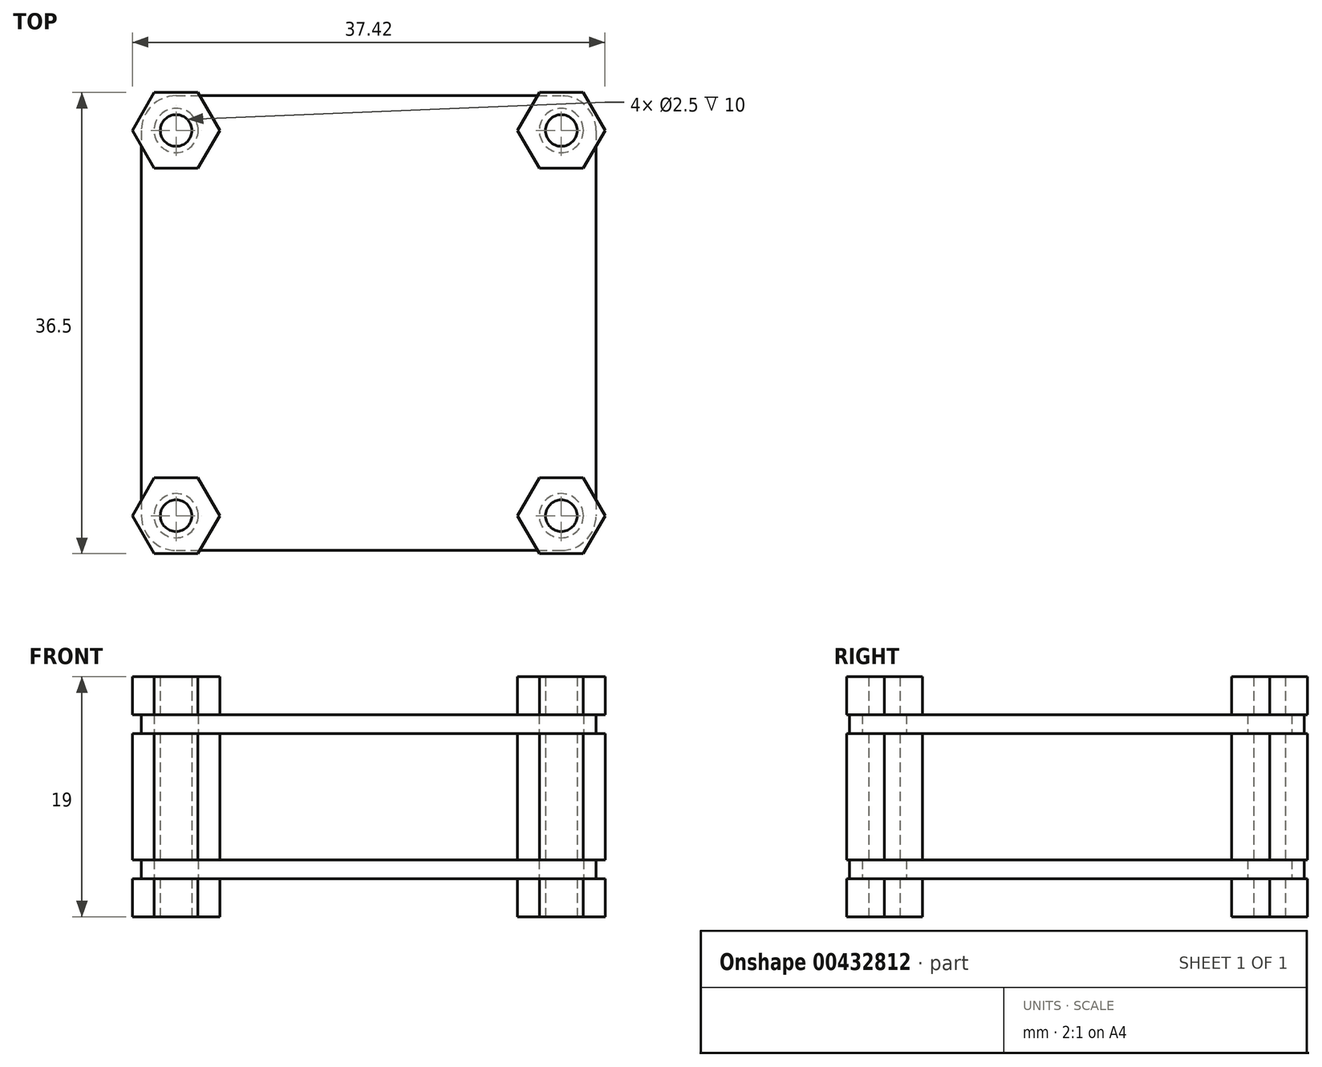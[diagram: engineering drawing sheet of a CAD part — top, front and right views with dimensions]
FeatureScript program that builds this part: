
annotation { "Feature Type Name" : "Feature", "Feature Type Description" : "" }
export const myFeature = defineFeature(function(context is Context, id is Id, definition is map)
    precondition{}
    {
        {
            var Q0;
            Q0=qCreatedBy(makeId("Top.planeOp"),FACE);
            var sketch = newSketch(context, id + "F0", { "sketchPlane" : qUnion([Q0])});
            skLineSegment(sketch, "E0.bottom", {"start": v(-15.25, 18) * mm, "end": v(15.25, 18) * mm});
            skLineSegment(sketch, "E0.top", {"start": v(-15.25, -18) * mm, "end": v(15.25, -18) * mm});
            skLineSegment(sketch, "E0.left", {"start": v(-18, 15.25) * mm, "end": v(-18, -15.25) * mm});
            skLineSegment(sketch, "E0.right", {"start": v(18, 15.25) * mm, "end": v(18, -15.25) * mm});
            skPoint(sketch, "E0.middle", {"position": v(0, 0) * mm});
            skPoint(sketch, "E1.visualSharp", {"position": v(-18, 18) * mm});
            skArc(sketch, "E1.filletArc", {"start": v(-15.25, 18) * mm, "mid": v(-17.2, 17.2) * mm, "end": v(-18, 15.25) * mm});
            skPoint(sketch, "E2.visualSharp", {"position": v(18, 18) * mm});
            skArc(sketch, "E2.filletArc", {"start": v(18, 15.25) * mm, "mid": v(17.2, 17.2) * mm, "end": v(15.25, 18) * mm});
            skPoint(sketch, "E3.visualSharp", {"position": v(18, -18) * mm});
            skArc(sketch, "E3.filletArc", {"start": v(15.25, -18) * mm, "mid": v(17.2, -17.2) * mm, "end": v(18, -15.25) * mm});
            skPoint(sketch, "E4.visualSharp", {"position": v(-18, -18) * mm});
            skArc(sketch, "E4.filletArc", {"start": v(-18, -15.25) * mm, "mid": v(-17.2, -17.2) * mm, "end": v(-15.25, -18) * mm});
            skCircle(sketch, "E5", {"center": v(-15.25, 15.25) * mm, "radius": 1.75 * mm});
            skCircle(sketch, "E6", {"center": v(15.25, 15.25) * mm, "radius": 1.75 * mm});
            skCircle(sketch, "E7", {"center": v(15.25, -15.25) * mm, "radius": 1.75 * mm});
            skCircle(sketch, "E8", {"center": v(-15.25, -15.25) * mm, "radius": 1.75 * mm});
            skSolve(sketch);
        }
        {
            var Q0;
            Q0=makeQuery(id+"F0.imprint","IMPRINT",FACE,{"disambiguationData":[TD([[makeQuery(id+"F0.imprint","IMPRINT",EDGE,{"derivedFrom":sQuery(id+"F0.wireOp",EDGE,"E0.bottom")}),-1.0]])]});
            extrude(context, id + "F1", {"entities" : qUnion([Q0]), "depth" : 4.5 * mm, "hasSecondDirection" : true, "secondDirectionOppositeDirection" : false, "secondDirectionDepth" : 3 * mm});
        }
        {
            var Q0;
            Q0=makeQuery(id+"F0.imprint","IMPRINT",FACE,{"disambiguationData":[TD([[makeQuery(id+"F0.imprint","IMPRINT",EDGE,{"derivedFrom":sQuery(id+"F0.wireOp",EDGE,"E0.bottom")}),-1.0]])]});
            extrude(context, id + "F2", {"entities" : qUnion([Q0]), "depth" : 16 * mm, "hasSecondDirection" : true, "secondDirectionOppositeDirection" : false, "secondDirectionDepth" : 14.5 * mm});
        }
        {
            var Q0;
            Q0=qCreatedBy(makeId("Top.planeOp"),FACE);
            var sketch = newSketch(context, id + "F3", { "sketchPlane" : qUnion([Q0])});
            skCircle(sketch, "E9.cCircle", {"center": v(-15.25, -15.25) * mm, "radius": 3 * mm, "construction": true});
            skLineSegment(sketch, "E9.0", {"start": v(-11.79, -15.25) * mm, "end": v(-13.52, -18.25) * mm});
            skLineSegment(sketch, "E9.1", {"start": v(-13.52, -18.25) * mm, "end": v(-16.98, -18.25) * mm});
            skLineSegment(sketch, "E9.2", {"start": v(-16.98, -18.25) * mm, "end": v(-18.71, -15.25) * mm});
            skLineSegment(sketch, "E9.3", {"start": v(-18.71, -15.25) * mm, "end": v(-16.98, -12.25) * mm});
            skLineSegment(sketch, "E9.4", {"start": v(-16.98, -12.25) * mm, "end": v(-13.52, -12.25) * mm});
            skLineSegment(sketch, "E9.5", {"start": v(-13.52, -12.25) * mm, "end": v(-11.79, -15.25) * mm});
            skPoint(sketch, "E9.0.midPoint", {"position": v(-12.65, -16.75) * mm});
            skLineSegment(sketch, "E10.MirrorCS", {"start": v(16.98, -12.25) * mm, "end": v(13.52, -12.25) * mm});
            skLineSegment(sketch, "E11.MirrorCS", {"start": v(18.71, -15.25) * mm, "end": v(16.98, -12.25) * mm});
            skLineSegment(sketch, "E12.MirrorCS", {"start": v(16.98, -18.25) * mm, "end": v(18.71, -15.25) * mm});
            skLineSegment(sketch, "E13.MirrorCS", {"start": v(13.52, -18.25) * mm, "end": v(16.98, -18.25) * mm});
            skLineSegment(sketch, "E14.MirrorCS", {"start": v(11.79, -15.25) * mm, "end": v(13.52, -18.25) * mm});
            skPoint(sketch, "E15.MirrorP", {"position": v(12.65, -16.75) * mm});
            skLineSegment(sketch, "E16.MirrorCS", {"start": v(13.52, -12.25) * mm, "end": v(11.79, -15.25) * mm});
            skCircle(sketch, "E17.MirrorC", {"center": v(15.25, -15.25) * mm, "radius": 3 * mm, "construction": true});
            skLineSegment(sketch, "E18.MirrorCS", {"start": v(11.79, 15.25) * mm, "end": v(13.52, 18.25) * mm});
            skLineSegment(sketch, "E19.MirrorCS", {"start": v(13.52, 18.25) * mm, "end": v(16.98, 18.25) * mm});
            skLineSegment(sketch, "E20.MirrorCS", {"start": v(16.98, 18.25) * mm, "end": v(18.71, 15.25) * mm});
            skLineSegment(sketch, "E21.MirrorCS", {"start": v(16.98, 12.25) * mm, "end": v(13.52, 12.25) * mm});
            skLineSegment(sketch, "E22.MirrorCS", {"start": v(-11.79, 15.25) * mm, "end": v(-13.52, 18.25) * mm});
            skLineSegment(sketch, "E23.MirrorCS", {"start": v(-13.52, 18.25) * mm, "end": v(-16.98, 18.25) * mm});
            skLineSegment(sketch, "E24.MirrorCS", {"start": v(-16.98, 18.25) * mm, "end": v(-18.71, 15.25) * mm});
            skLineSegment(sketch, "E25.MirrorCS", {"start": v(-16.98, 12.25) * mm, "end": v(-13.52, 12.25) * mm});
            skLineSegment(sketch, "E26.MirrorCS", {"start": v(-13.52, 12.25) * mm, "end": v(-11.79, 15.25) * mm});
            skPoint(sketch, "E27.MirrorP", {"position": v(-12.65, 16.75) * mm});
            skPoint(sketch, "E28.MirrorP", {"position": v(12.65, 16.75) * mm});
            skCircle(sketch, "E29.MirrorC", {"center": v(15.25, 15.25) * mm, "radius": 3 * mm, "construction": true});
            skLineSegment(sketch, "E30.MirrorCS", {"start": v(13.52, 12.25) * mm, "end": v(11.79, 15.25) * mm});
            skLineSegment(sketch, "E31.MirrorCS", {"start": v(18.71, 15.25) * mm, "end": v(16.98, 12.25) * mm});
            skCircle(sketch, "E32.MirrorC", {"center": v(-15.25, 15.25) * mm, "radius": 3 * mm, "construction": true});
            skLineSegment(sketch, "E33.MirrorCS", {"start": v(-18.71, 15.25) * mm, "end": v(-16.98, 12.25) * mm});
            skCircle(sketch, "E34", {"center": v(-15.25, -15.25) * mm, "radius": 1.25 * mm});
            skCircle(sketch, "E35", {"center": v(15.25, -15.25) * mm, "radius": 1.25 * mm});
            skCircle(sketch, "E36", {"center": v(15.25, 15.25) * mm, "radius": 1.25 * mm});
            skCircle(sketch, "E37", {"center": v(-15.25, 15.25) * mm, "radius": 1.25 * mm});
            skSolve(sketch);
        }
        {
            var Q0;
            Q0 = qSketchRegion(id + "F3", true);
            extrude(context, id + "F4", {"entities" : qUnion([Q0]), "operationType" : NewBodyOperationType.ADD, "depth" : 3 * mm});
        }
        {
            var Q0;
            Q0 = qSketchRegion(id + "F3", true);
            extrude(context, id + "F5", {"entities" : qUnion([Q0]), "operationType" : NewBodyOperationType.ADD, "depth" : 14.5 * mm, "hasSecondDirection" : true, "secondDirectionOppositeDirection" : false, "secondDirectionDepth" : 4.5 * mm});
        }
        {
            var Q0;
            Q0 = qSketchRegion(id + "F3", true);
            extrude(context, id + "F6", {"entities" : qUnion([Q0]), "operationType" : NewBodyOperationType.ADD, "depth" : 19 * mm, "hasSecondDirection" : true, "secondDirectionOppositeDirection" : false, "secondDirectionDepth" : 16 * mm});
        }
    });
